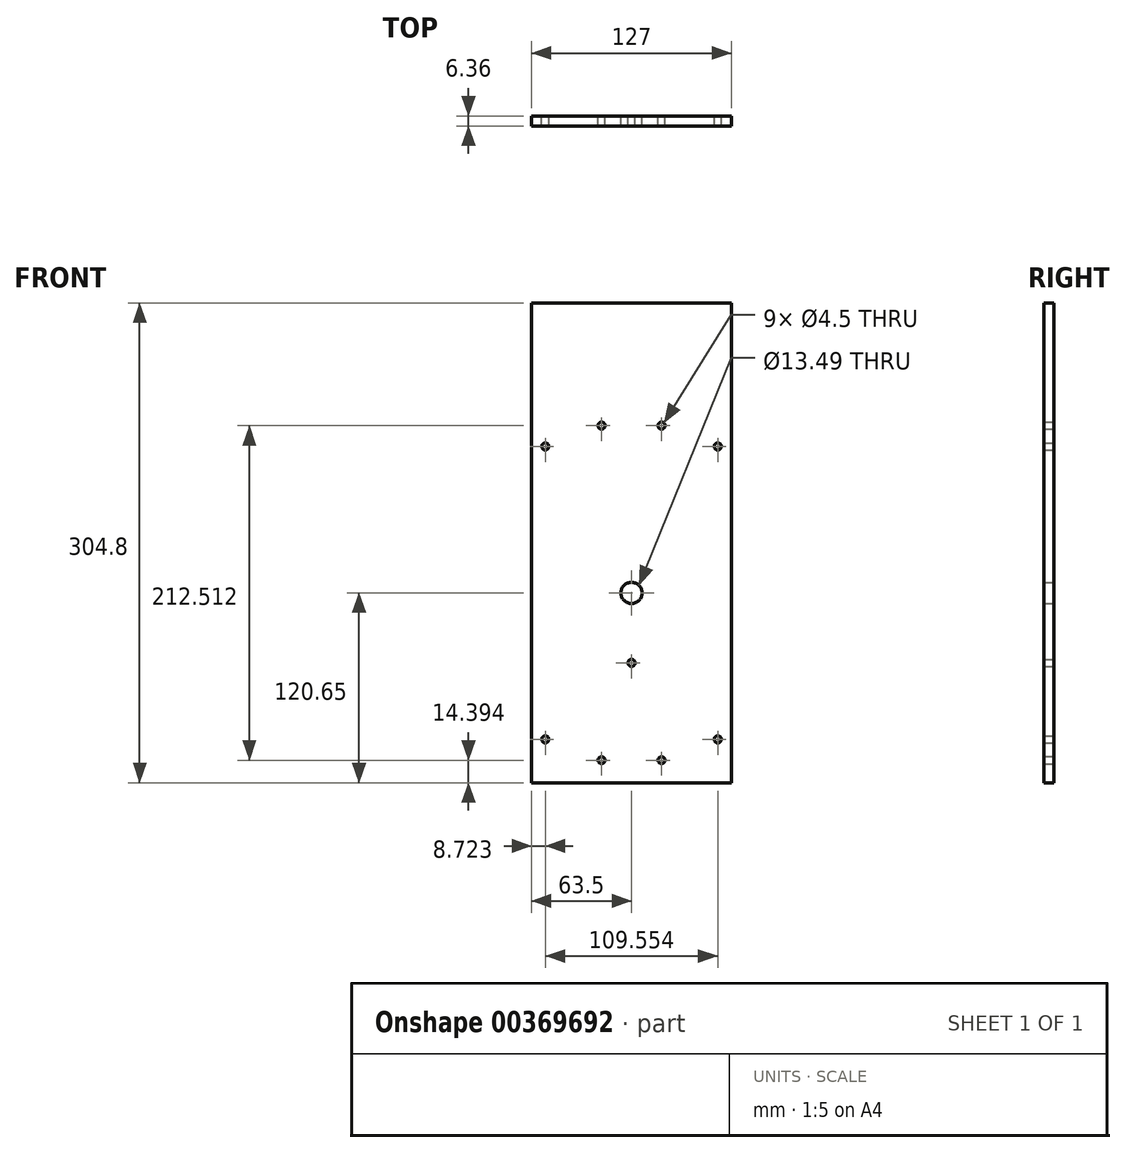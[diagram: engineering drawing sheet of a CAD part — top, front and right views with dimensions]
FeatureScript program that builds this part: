
annotation { "Feature Type Name" : "Feature", "Feature Type Description" : "" }
export const myFeature = defineFeature(function(context is Context, id is Id, definition is map)
    precondition{}
    {
        {
            var Q0;
            Q0=qCreatedBy(makeId("Top.planeOp"),FACE);
            var sketch = newSketch(context, id + "F0", { "sketchPlane" : qUnion([Q0])});
            skLineSegment(sketch, "E0.bottom", {"start": v(-63.5, 3.18) * mm, "end": v(63.5, 3.17) * mm});
            skLineSegment(sketch, "E0.top", {"start": v(-63.5, -3.17) * mm, "end": v(63.5, -3.18) * mm});
            skLineSegment(sketch, "E0.left", {"start": v(-63.5, 3.17) * mm, "end": v(-63.5, -3.17) * mm});
            skLineSegment(sketch, "E0.right", {"start": v(63.5, 3.17) * mm, "end": v(63.5, -3.17) * mm});
            skSolve(sketch);
        }
        {
            var Q0;
            Q0 = qSketchRegion(id + "F0", true);
            extrude(context, id + "F1", {"entities" : qUnion([Q0]), "endBound" : BoundingType.SYMMETRIC, "depth" : 304.8 * mm, "offsetDistance" : 25.4 * mm});
        }
        {
            var Q0;
            Q0=makeQuery(id+"F1.opExtrude","SWEPT_FACE",FACE,{"disambiguationData":[OSD([sQuery(id+"F0.wireOp",EDGE,"E0.bottom")])]});
            var sketch = newSketch(context, id + "F2", { "sketchPlane" : qUnion([Q0])});
            skLineSegment(sketch, "E1.0", {"start": v(63.5, -152.4) * mm, "end": v(-63.5, -152.4) * mm, "construction": true});
            skLineSegment(sketch, "E2", {"start": v(63.5, -139.7) * mm, "end": v(-63.5, -139.7) * mm, "construction": true});
            skLineSegment(sketch, "E3", {"start": v(63.5, -31.75) * mm, "end": v(-63.5, -31.75) * mm, "construction": true});
            skLineSegment(sketch, "E4", {"start": v(0, -31.75) * mm, "end": v(0, -139.7) * mm, "construction": true});
            skCircle(sketch, "E5", {"center": v(0, -31.75) * mm, "radius": 107.95 * mm, "construction": true});
            skPoint(sketch, "E6", {"position": v(-19.05, -138) * mm});
            skPoint(sketch, "E7", {"position": v(19.05, -138) * mm});
            skPoint(sketch, "E8", {"position": v(54.78, -124.77) * mm});
            skPoint(sketch, "E9", {"position": v(-54.78, -124.77) * mm});
            skLineSegment(sketch, "E10", {"start": v(19.05, -138) * mm, "end": v(0, -31.75) * mm, "construction": true});
            skLineSegment(sketch, "E11", {"start": v(-19.05, -138) * mm, "end": v(0, -31.75) * mm, "construction": true});
            skLineSegment(sketch, "E12", {"start": v(-54.78, -124.77) * mm, "end": v(0, -31.75) * mm, "construction": true});
            skLineSegment(sketch, "E13", {"start": v(54.78, -124.77) * mm, "end": v(0, -31.75) * mm, "construction": true});
            skLineSegment(sketch, "E14", {"start": v(19.05, -138) * mm, "end": v(-19.05, -138) * mm, "construction": true});
            skLineSegment(sketch, "E15", {"start": v(-19.05, -138) * mm, "end": v(-54.78, -124.77) * mm, "construction": true});
            skLineSegment(sketch, "E16", {"start": v(19.05, -138) * mm, "end": v(54.78, -124.77) * mm, "construction": true});
            skPoint(sketch, "E17.MirrorP", {"position": v(54.78, 61.27) * mm});
            skPoint(sketch, "E18.MirrorP", {"position": v(-54.78, 61.27) * mm});
            skPoint(sketch, "E19.MirrorP", {"position": v(-19.05, 74.5) * mm});
            skPoint(sketch, "E20.MirrorP", {"position": v(19.05, 74.5) * mm});
            skLineSegment(sketch, "E21.MirrorCS", {"start": v(-19.05, 74.5) * mm, "end": v(-54.78, 61.27) * mm, "construction": true});
            skLineSegment(sketch, "E22.MirrorCS", {"start": v(19.05, 74.5) * mm, "end": v(-19.05, 74.5) * mm, "construction": true});
            skLineSegment(sketch, "E23.MirrorCS", {"start": v(19.05, 74.5) * mm, "end": v(54.78, 61.27) * mm, "construction": true});
            skLineSegment(sketch, "E24.MirrorCS", {"start": v(54.78, 61.27) * mm, "end": v(0, -31.75) * mm, "construction": true});
            skLineSegment(sketch, "E25.MirrorCS", {"start": v(-54.78, 61.27) * mm, "end": v(0, -31.75) * mm, "construction": true});
            skLineSegment(sketch, "E26.MirrorCS", {"start": v(19.05, 74.5) * mm, "end": v(0, -31.75) * mm, "construction": true});
            skLineSegment(sketch, "E27.MirrorCS", {"start": v(-19.05, 74.5) * mm, "end": v(0, -31.75) * mm, "construction": true});
            skPoint(sketch, "E28", {"position": v(0, -76.2) * mm});
            skSolve(sketch);
        }
        {
            var Q0;
            Q0=sQuery(id+"F2.wireOp",VERTEX,"E8");
            var Q1;
            Q1=sQuery(id+"F2.wireOp",VERTEX,"E7");
            var Q2;
            Q2=sQuery(id+"F2.wireOp",VERTEX,"E6");
            var Q3;
            Q3=sQuery(id+"F2.wireOp",VERTEX,"E9");
            var Q4;
            Q4=sQuery(id+"F2.wireOp",VERTEX,"E17.MirrorP");
            var Q5;
            Q5=sQuery(id+"F2.wireOp",VERTEX,"E20.MirrorP");
            var Q6;
            Q6=sQuery(id+"F2.wireOp",VERTEX,"E19.MirrorP");
            var Q7;
            Q7=sQuery(id+"F2.wireOp",VERTEX,"E18.MirrorP");
            var Q8;
            Q8=makeQuery(id+"F1.opExtrude","SWEPT_BODY",BODY,{"disambiguationData":[OSD([sQuery(id+"F0.wireOp",EDGE,"E0.bottom"),sQuery(id+"F0.wireOp",EDGE,"E0.top"),sQuery(id+"F0.wireOp",EDGE,"E0.left"),sQuery(id+"F0.wireOp",EDGE,"E0.right")])]});
            hole(context, id + "F3", {"style" : HoleStyle.SIMPLE, "endStyle" : HoleEndStyle.THROUGH, "standardTappedOrClearance" : lookupTablePath({ "standard" : "ANSI", "fit" : "Normal (ASME)", "size" : "#8", "type" : "Clearance" }), "standardBlindInLast" : lookupTablePath({ "fit" : "Free", "standard" : "ANSI", "size" : "#8", "type" : "Clearance" }), "holeDiameter" : 4.5 * mm, "majorDiameter" : 6.35 * mm, "tappedDepth" : 9.52 * mm, "tapClearance" : 3, "startFromSketch" : true, "locations" : qUnion([Q0, Q1, Q2, Q3, Q4, Q5, Q6, Q7]), "scope" : qUnion([Q8])});
        }
        {
            var Q0;
            Q0=sQuery(id+"F2.wireOp",VERTEX,"E5.center");
            var Q1;
            Q1=makeQuery(id+"F1.opExtrude","SWEPT_BODY",BODY,{"disambiguationData":[OSD([sQuery(id+"F0.wireOp",EDGE,"E0.bottom"),sQuery(id+"F0.wireOp",EDGE,"E0.top"),sQuery(id+"F0.wireOp",EDGE,"E0.left"),sQuery(id+"F0.wireOp",EDGE,"E0.right")])]});
            hole(context, id + "F4", {"style" : HoleStyle.SIMPLE, "endStyle" : HoleEndStyle.THROUGH, "standardTappedOrClearance" : lookupTablePath({ "standard" : "ANSI", "fit" : "Normal (ASME)", "size" : "1/2", "type" : "Clearance" }), "standardBlindInLast" : lookupTablePath({ "fit" : "Free", "standard" : "ANSI", "size" : "1/2", "type" : "Clearance" }), "holeDiameter" : 13.5 * mm, "majorDiameter" : 6.35 * mm, "tappedDepth" : 9.52 * mm, "tapClearance" : 3, "startFromSketch" : true, "locations" : qUnion([Q0]), "scope" : qUnion([Q1])});
        }
        {
            var Q0;
            Q0=sQuery(id+"F2.wireOp",VERTEX,"E28");
            var Q1;
            Q1=makeQuery(id+"F1.opExtrude","SWEPT_BODY",BODY,{"disambiguationData":[OSD([sQuery(id+"F0.wireOp",EDGE,"E0.bottom"),sQuery(id+"F0.wireOp",EDGE,"E0.top"),sQuery(id+"F0.wireOp",EDGE,"E0.left"),sQuery(id+"F0.wireOp",EDGE,"E0.right")])]});
            hole(context, id + "F5", {"style" : HoleStyle.SIMPLE, "endStyle" : HoleEndStyle.THROUGH, "standardTappedOrClearance" : lookupTablePath({ "standard" : "ANSI", "fit" : "Normal (ASME)", "size" : "#8", "type" : "Clearance" }), "standardBlindInLast" : lookupTablePath({ "fit" : "Free", "standard" : "ANSI", "size" : "#8", "type" : "Clearance" }), "holeDiameter" : 4.5 * mm, "majorDiameter" : 6.35 * mm, "tappedDepth" : 9.52 * mm, "tapClearance" : 3, "startFromSketch" : true, "locations" : qUnion([Q0]), "scope" : qUnion([Q1])});
        }
    });
